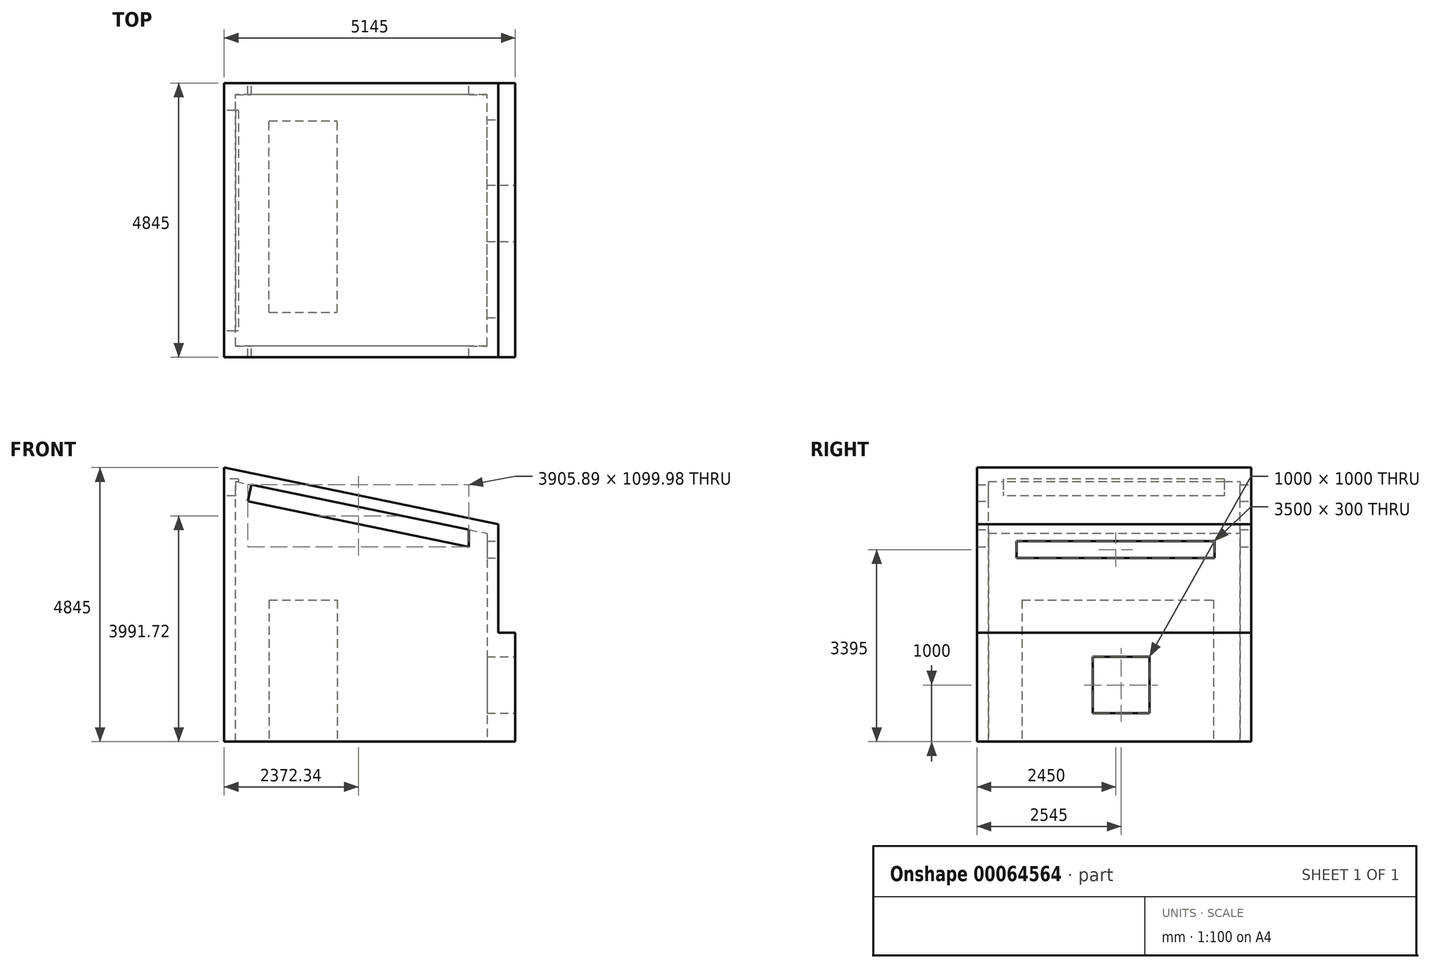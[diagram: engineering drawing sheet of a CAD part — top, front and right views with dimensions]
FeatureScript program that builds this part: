
annotation { "Feature Type Name" : "Feature", "Feature Type Description" : "" }
export const myFeature = defineFeature(function(context is Context, id is Id, definition is map)
    precondition{}
    {
        {
            var Q0;
            Q0=qCreatedBy(makeId("Front.planeOp"),FACE);
            var sketch = newSketch(context, id + "F0", { "sketchPlane" : qUnion([Q0])});
            skLineSegment(sketch, "E0", {"start": v(0, 0) * mm, "end": v(0, 4845) * mm});
            skLineSegment(sketch, "E1", {"start": v(0, 4845) * mm, "end": v(4845, 3845) * mm});
            skLineSegment(sketch, "E2", {"start": v(4845, 3845) * mm, "end": v(4845, 0) * mm});
            skLineSegment(sketch, "E3", {"start": v(4845, 0) * mm, "end": v(0, 0) * mm});
            skSolve(sketch);
        }
        {
            var Q0;
            Q0 = qSketchRegion(id + "F0", true);
            extrude(context, id + "F1", {"entities" : qUnion([Q0]), "depth" : 4845 * mm});
        }
        {
            var Q0;
            Q0=makeQuery(id+"F1.opExtrude","SWEPT_FACE",FACE,{"disambiguationData":[OSD([sQuery(id+"F0.wireOp",EDGE,"E3")])]});
            shell(context, id + "F2", {"entities" : qUnion([Q0]), "thickness" : 200 * mm});
        }
        {
            var Q0;
            Q0=makeQuery(id+"F1.opExtrude","CAP_FACE",FACE,{"disambiguationData":[OSD([sQuery(id+"F0.wireOp",EDGE,"E0"),sQuery(id+"F0.wireOp",EDGE,"E1"),sQuery(id+"F0.wireOp",EDGE,"E2"),sQuery(id+"F0.wireOp",EDGE,"E3")])],"isStart":true});
            var sketch = newSketch(context, id + "F3", { "sketchPlane" : qUnion([Q0])});
            skLineSegment(sketch, "E4", {"start": v(-4325.28, 3748.05) * mm, "end": v(-480.03, 4541.7) * mm});
            skLineSegment(sketch, "E5", {"start": v(-480.03, 4541.7) * mm, "end": v(-419.4, 4247.9) * mm});
            skLineSegment(sketch, "E6", {"start": v(-419.4, 4247.9) * mm, "end": v(-4325.28, 3441.73) * mm});
            skLineSegment(sketch, "E7", {"start": v(-4325.28, 3441.73) * mm, "end": v(-4325.28, 3748.05) * mm});
            skSolve(sketch);
        }
        {
            var Q0;
            Q0 = qSketchRegion(id + "F3", true);
            extrude(context, id + "F4", {"entities" : qUnion([Q0]), "operationType" : NewBodyOperationType.REMOVE, "endBound" : BoundingType.THROUGH_ALL, "oppositeDirection" : true, "depth" : 25 * mm});
        }
        {
            var Q0;
            Q0=makeQuery(id+"F1.opExtrude","SWEPT_FACE",FACE,{"disambiguationData":[OSD([sQuery(id+"F0.wireOp",EDGE,"E0")])]});
            var sketch = newSketch(context, id + "F5", { "sketchPlane" : qUnion([Q0])});
            skLineSegment(sketch, "E8.bottom", {"start": v(480, 4645) * mm, "end": v(4380, 4645) * mm});
            skLineSegment(sketch, "E8.top", {"start": v(480, 4345) * mm, "end": v(4380, 4345) * mm});
            skLineSegment(sketch, "E8.left", {"start": v(480, 4645) * mm, "end": v(480, 4345) * mm});
            skLineSegment(sketch, "E8.right", {"start": v(4380, 4645) * mm, "end": v(4380, 4345) * mm});
            skSolve(sketch);
        }
        {
            var Q0;
            Q0 = qSketchRegion(id + "F5", true);
            extrude(context, id + "F6", {"entities" : qUnion([Q0]), "operationType" : NewBodyOperationType.REMOVE, "oppositeDirection" : true, "depth" : 250 * mm});
        }
        {
            var Q0;
            Q0=makeQuery(id+"F1.opExtrude","SWEPT_FACE",FACE,{"disambiguationData":[OSD([sQuery(id+"F0.wireOp",EDGE,"E2")])]});
            var sketch = newSketch(context, id + "F7", { "sketchPlane" : qUnion([Q0])});
            skLineSegment(sketch, "E9.bottom", {"start": v(-4845, 0) * mm, "end": v(0, 0) * mm});
            skLineSegment(sketch, "E9.top", {"start": v(-4845, 1922.5) * mm, "end": v(0, 1922.5) * mm});
            skLineSegment(sketch, "E9.left", {"start": v(-4845, 0) * mm, "end": v(-4845, 1922.5) * mm});
            skLineSegment(sketch, "E9.right", {"start": v(0, 0) * mm, "end": v(0, 1922.5) * mm});
            skSolve(sketch);
        }
        {
            var Q0;
            Q0 = qSketchRegion(id + "F7", true);
            extrude(context, id + "F8", {"entities" : qUnion([Q0]), "operationType" : NewBodyOperationType.ADD, "depth" : 300 * mm});
        }
        {
            var Q0;
            Q0=makeQuery(id+"F8.opExtrude","CAP_FACE",FACE,{"disambiguationData":[OSD([sQuery(id+"F7.wireOp",EDGE,"E9.bottom"),sQuery(id+"F7.wireOp",EDGE,"E9.top"),sQuery(id+"F7.wireOp",EDGE,"E9.left"),sQuery(id+"F7.wireOp",EDGE,"E9.right")])],"isStart":false});
            var sketch = newSketch(context, id + "F9", { "sketchPlane" : qUnion([Q0])});
            skLineSegment(sketch, "E10.bottom", {"start": v(-2800, 1500) * mm, "end": v(-1800, 1500) * mm});
            skLineSegment(sketch, "E10.top", {"start": v(-2800, 500) * mm, "end": v(-1800, 500) * mm});
            skLineSegment(sketch, "E10.left", {"start": v(-2800, 1500) * mm, "end": v(-2800, 500) * mm});
            skLineSegment(sketch, "E10.right", {"start": v(-1800, 1500) * mm, "end": v(-1800, 500) * mm});
            skSolve(sketch);
        }
        {
            var Q0;
            Q0 = qSketchRegion(id + "F9", true);
            extrude(context, id + "F10", {"entities" : qUnion([Q0]), "operationType" : NewBodyOperationType.REMOVE, "oppositeDirection" : true, "depth" : 500 * mm});
        }
        {
            var Q0;
            Q0=makeQuery(id+"F1.opExtrude","SWEPT_FACE",FACE,{"disambiguationData":[OSD([sQuery(id+"F0.wireOp",EDGE,"E2")])]});
            var sketch = newSketch(context, id + "F11", { "sketchPlane" : qUnion([Q0])});
            skLineSegment(sketch, "E11.bottom", {"start": v(-4145, 3545) * mm, "end": v(-645, 3545) * mm});
            skLineSegment(sketch, "E11.top", {"start": v(-4145, 3245) * mm, "end": v(-645, 3245) * mm});
            skLineSegment(sketch, "E11.left", {"start": v(-4145, 3545) * mm, "end": v(-4145, 3245) * mm});
            skLineSegment(sketch, "E11.right", {"start": v(-645, 3545) * mm, "end": v(-645, 3245) * mm});
            skSolve(sketch);
        }
        {
            var Q0;
            Q0 = qSketchRegion(id + "F11", true);
            extrude(context, id + "F12", {"entities" : qUnion([Q0]), "operationType" : NewBodyOperationType.REMOVE, "oppositeDirection" : true, "depth" : 350 * mm});
        }
        {
            var Q0;
            Q0=qCreatedBy(makeId("Top.planeOp"),FACE);
            var sketch = newSketch(context, id + "F13", { "sketchPlane" : qUnion([Q0])});
            skLineSegment(sketch, "E12.bottom", {"start": v(795.2, -4052.14) * mm, "end": v(1996.46, -4052.14) * mm});
            skLineSegment(sketch, "E12.top", {"start": v(795.2, -668.3) * mm, "end": v(1996.46, -668.3) * mm});
            skLineSegment(sketch, "E12.left", {"start": v(795.2, -4052.14) * mm, "end": v(795.2, -668.3) * mm});
            skLineSegment(sketch, "E12.right", {"start": v(1996.46, -4052.14) * mm, "end": v(1996.46, -668.3) * mm});
            skSolve(sketch);
        }
        {
            var Q0;
            Q0 = qSketchRegion(id + "F13", true);
            extrude(context, id + "F14", {"entities" : qUnion([Q0]), "depth" : 2500 * mm});
        }
    });
